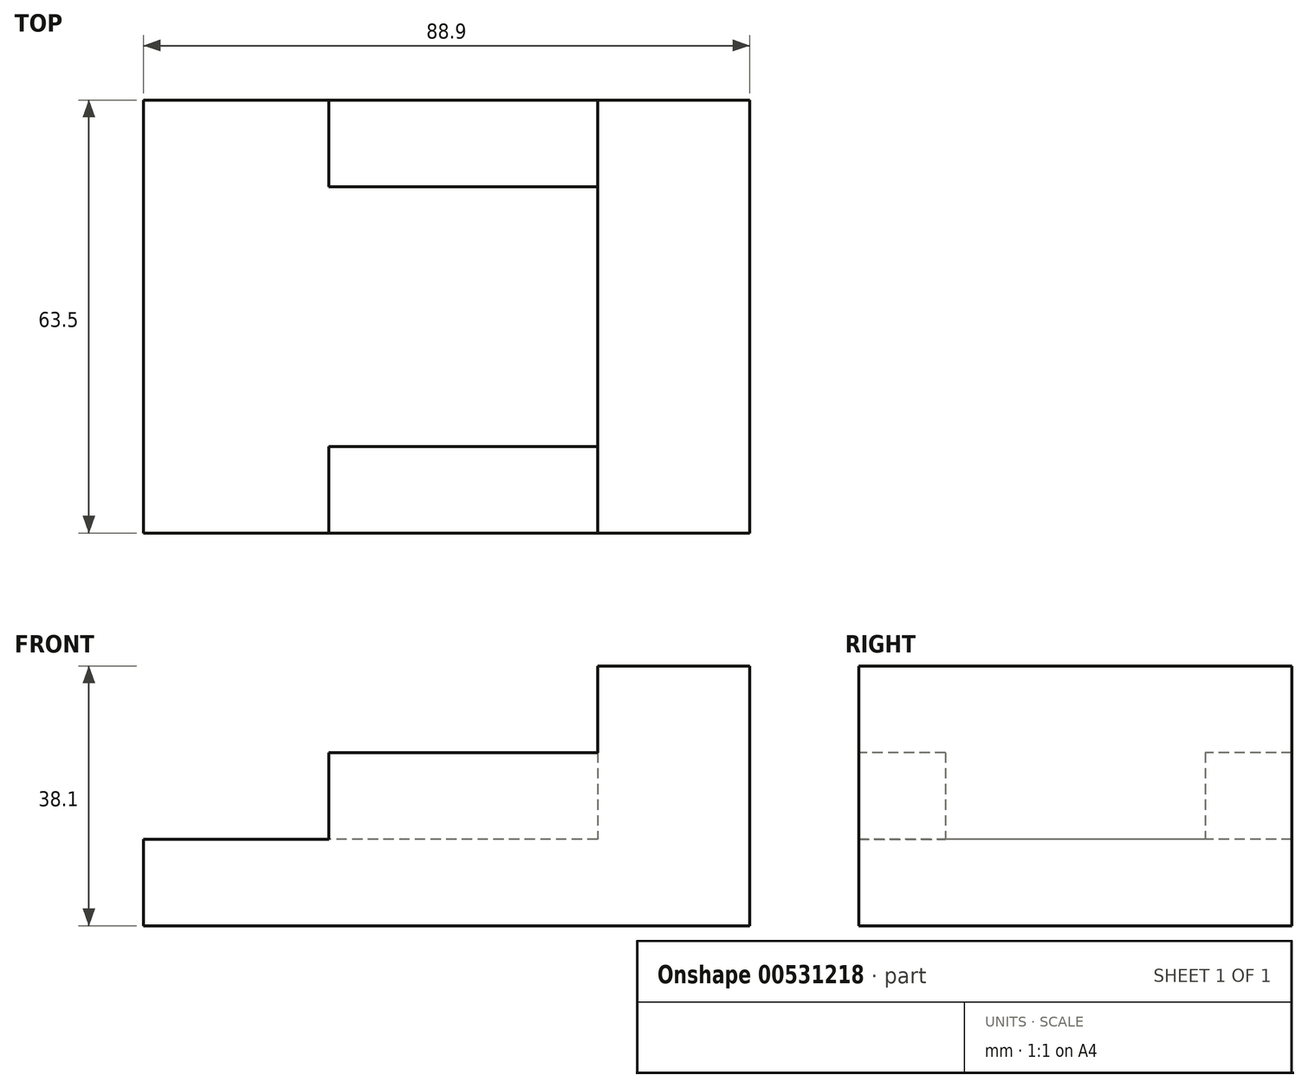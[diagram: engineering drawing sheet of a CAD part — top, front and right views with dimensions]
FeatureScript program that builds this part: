
annotation { "Feature Type Name" : "Feature", "Feature Type Description" : "" }
export const myFeature = defineFeature(function(context is Context, id is Id, definition is map)
    precondition{}
    {
        {
            var Q0;
            Q0=qCreatedBy(makeId("Top.planeOp"),FACE);
            var sketch = newSketch(context, id + "F0", { "sketchPlane" : qUnion([Q0])});
            skLineSegment(sketch, "E0.bottom", {"start": v(-44.45, 31.75) * mm, "end": v(44.45, 31.75) * mm});
            skLineSegment(sketch, "E0.top", {"start": v(-44.45, -31.75) * mm, "end": v(44.45, -31.75) * mm});
            skLineSegment(sketch, "E0.left", {"start": v(-44.45, 31.75) * mm, "end": v(-44.45, -31.75) * mm});
            skLineSegment(sketch, "E0.right", {"start": v(44.45, 31.75) * mm, "end": v(44.45, -31.75) * mm});
            skPoint(sketch, "E0.middle", {"position": v(0, 0) * mm});
            skSolve(sketch);
        }
        {
            var Q0;
            Q0=makeQuery(id+"F0.imprint","IMPRINT",FACE,{"disambiguationData":[TD([[makeQuery(id+"F0.imprint","IMPRINT",EDGE,{"derivedFrom":sQuery(id+"F0.wireOp",EDGE,"E0.bottom")}),-1.0]])]});
            extrude(context, id + "F1", {"entities" : qUnion([Q0]), "depth" : 12.7 * mm, "offsetDistance" : 25.4 * mm});
        }
        {
            var Q0;
            Q0=makeQuery(id+"F1.opExtrude","CAP_FACE",FACE,{"disambiguationData":[OSD([sQuery(id+"F0.wireOp",EDGE,"E0.bottom"),sQuery(id+"F0.wireOp",EDGE,"E0.top"),sQuery(id+"F0.wireOp",EDGE,"E0.left"),sQuery(id+"F0.wireOp",EDGE,"E0.right")])],"isStart":false});
            var sketch = newSketch(context, id + "F2", { "sketchPlane" : qUnion([Q0])});
            skLineSegment(sketch, "E1.bottom", {"start": v(44.45, 31.75) * mm, "end": v(22.15, 31.75) * mm});
            skLineSegment(sketch, "E1.top", {"start": v(44.45, -31.75) * mm, "end": v(22.15, -31.75) * mm});
            skLineSegment(sketch, "E1.left", {"start": v(44.45, 31.75) * mm, "end": v(44.45, -31.75) * mm});
            skLineSegment(sketch, "E1.right", {"start": v(22.15, 31.75) * mm, "end": v(22.15, -31.75) * mm});
            skSolve(sketch);
        }
        {
            var Q0;
            Q0=makeQuery(id+"F2.imprint","IMPRINT",FACE,{"disambiguationData":[TD([[makeQuery(id+"F2.imprint","IMPRINT",EDGE,{"derivedFrom":sQuery(id+"F2.wireOp",EDGE,"E1.bottom")}),-1.0]])]});
            extrude(context, id + "F3", {"entities" : qUnion([Q0]), "operationType" : NewBodyOperationType.ADD, "depth" : 25.4 * mm, "offsetDistance" : 25.4 * mm});
        }
        {
            var Q0;
            Q0=makeQuery(id+"F1.opExtrude","CAP_FACE",FACE,{"disambiguationData":[OSD([sQuery(id+"F0.wireOp",EDGE,"E0.bottom"),sQuery(id+"F0.wireOp",EDGE,"E0.top"),sQuery(id+"F0.wireOp",EDGE,"E0.left"),sQuery(id+"F0.wireOp",EDGE,"E0.right")])],"isStart":false});
            var sketch = newSketch(context, id + "F4", { "sketchPlane" : qUnion([Q0])});
            skLineSegment(sketch, "E2.bottom", {"start": v(22.15, 31.75) * mm, "end": v(-17.26, 31.75) * mm});
            skLineSegment(sketch, "E2.top", {"start": v(22.15, 19.05) * mm, "end": v(-17.26, 19.05) * mm});
            skLineSegment(sketch, "E2.left", {"start": v(22.15, 31.75) * mm, "end": v(22.15, 19.05) * mm});
            skLineSegment(sketch, "E2.right", {"start": v(-17.26, 31.75) * mm, "end": v(-17.26, 19.05) * mm});
            skLineSegment(sketch, "E3.bottom", {"start": v(22.15, -31.75) * mm, "end": v(-17.26, -31.75) * mm});
            skLineSegment(sketch, "E3.top", {"start": v(22.15, -19.05) * mm, "end": v(-17.26, -19.05) * mm});
            skLineSegment(sketch, "E3.left", {"start": v(22.15, -31.75) * mm, "end": v(22.15, -19.05) * mm});
            skLineSegment(sketch, "E3.right", {"start": v(-17.26, -31.75) * mm, "end": v(-17.26, -19.05) * mm});
            skSolve(sketch);
        }
        {
            var Q0;
            Q0=makeQuery(id+"F4.imprint","IMPRINT",FACE,{"disambiguationData":[TD([[makeQuery(id+"F4.imprint","IMPRINT",EDGE,{"derivedFrom":sQuery(id+"F4.wireOp",EDGE,"E2.bottom")}),-1.0]])]});
            var Q1;
            Q1=makeQuery(id+"F4.imprint","IMPRINT",FACE,{"disambiguationData":[TD([[makeQuery(id+"F4.imprint","IMPRINT",EDGE,{"derivedFrom":sQuery(id+"F4.wireOp",EDGE,"E3.bottom")}),1.0]])]});
            extrude(context, id + "F5", {"entities" : qUnion([Q0, Q1]), "operationType" : NewBodyOperationType.ADD, "depth" : 12.7 * mm, "offsetDistance" : 25.4 * mm});
        }
    });
